# Revit family: ElectricalEquipment_Hager_TPNLighting&Power_HagerTPNExtBoxContactorIncomers
name_source: partatom
category: Electrical Equipment
revit_build: Autodesk Revit 2015 (Build: 20160512_1515(x64)
units: mm (PartAtom-declared; Revit-internal decimal feet)

## types (3) — shared parameters
CE Approval = Yes
Colour = BS4800:2011 00A01 Oyster Grey
Default Elevation = 1200 mm
Design Country = China
Door = 46 mm  [stored 0.150919 ft]
Door Type = Single Plain Door
Enclosure Rating = IP3X
Frequency = 50 Hz
Location = Indoors
Location of Manufacturer = Telford, TF1 7FT
MCB Rating = 63 A
Mains Type = 3 phase
Manufacturer = Hager UK Ltd
Manufacturer Country = United Kingdom
Manufacturer Website = www.hager.co.uk
Neutral Rating = 100.00%
Number of Poles = 4
Overall Width = 465 mm  [stored 1.52559 ft]
Packaging Recyclable = Yes
Packaging Weight = 1.00 kg
Pollution Degree = 2
Product Family = TPN Ext Box Contactor Incomer
Product Group = TPN
Product Range = Invicta 3 TPN Contacor Incomer
Reference Standard = BS EN 61439-3
Revision = 2
Shape = Rectangular
Supply Phase = 1,3
Type = ElectricalFixture
URL = www.hager.co.uk
Ui Rating = 690 V
Uimp Rating = 4000 V
Voltage = 415
Warranty ID = 24 Months
zero-valued in all types: Max #3 Pole Breakers, Outging Ways (TP)

## per-type parameters (varying)
| type | Busbar Rating | Description | EAN | Hager Catalogue Ref | Model | Overall Height | Product Description | Product Literature | Product Weight | Type Comments |
| TPN Ext Box Contactor Incomer 63A AC23 | 63 A | JK1 TPN Contactor Incomer 63A 4P AC23 | 5015652250241 | JK10634C | JK10634C | 166 mm  [stored 0.544619 ft] | JK1 TPN Contactor Incomer 63A 4P AC23 | www.hager.co.uk/?artnr=JK10634C | 14.50 kg | Mounted directly below JK1 primary Distribution Board |
| TPN Ext Box Contactor Incomer 100A AC23 | 100 A | JK1 TPN Contactor Incomer 100A 4P AC23 | 5015652250302 | JK11004C | JK11004C | 235 mm  [stored 0.770997 ft] | JK1 TPN Contactor Incomer 100A 4P AC23 | www.hager.co.uk/?artnr=JK11004C | 16.50 kg | Mounted directly below JK1 primary Distribution Board |
| TPN Ext Box Contactor Incomer 160A AC23 | 160 A | JK2 TPN Contactor Incomer 160A 4P AC23 | 5015652250524 | JK21604C | JK21604C | 235 mm  [stored 0.770997 ft] | JK2 TPN Contactor Incomer 160A 4P AC23 | www.hager.co.uk/?artnr=JK21604C | 16.50 kg | Mounted directly below JK2 primary Distribution Board |

note: [stored X ft] marks values corroborated as IEEE doubles in the binary element streams (Revit-internal decimal feet)

## geometry (parser evidence)
native form markers: Sweep x3
no freeform markers — native parametric forms only
